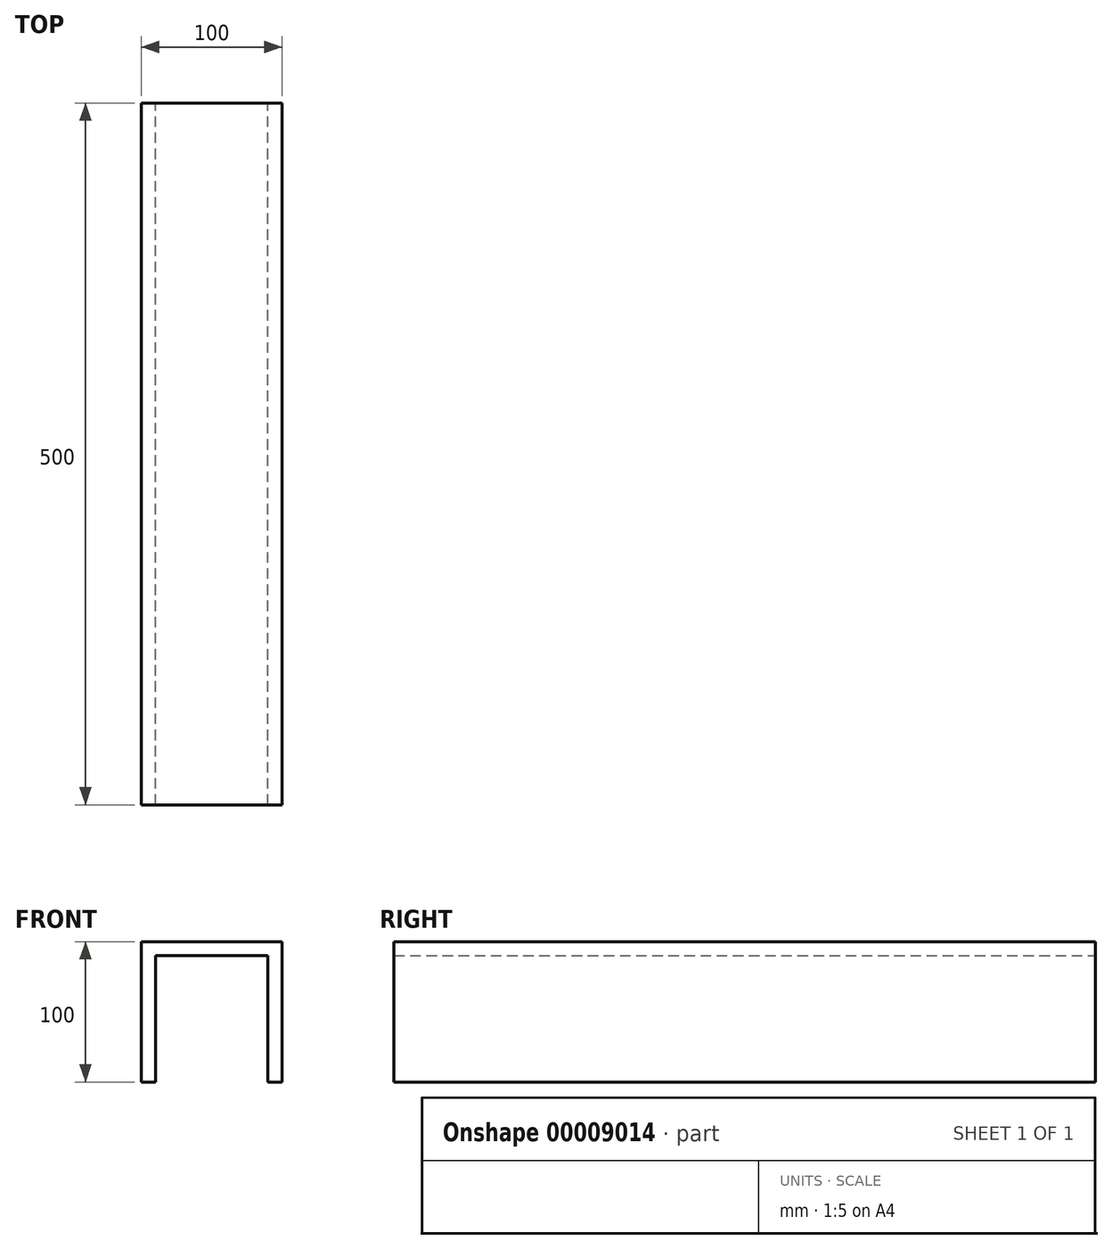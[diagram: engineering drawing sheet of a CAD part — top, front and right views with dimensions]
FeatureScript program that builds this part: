
annotation { "Feature Type Name" : "Feature", "Feature Type Description" : "" }
export const myFeature = defineFeature(function(context is Context, id is Id, definition is map)
    precondition{}
    {
        {
            var Q0;
            Q0=qCreatedBy(makeId("Front.planeOp"),FACE);
            var sketch = newSketch(context, id + "F0", { "sketchPlane" : qUnion([Q0])});
            skLineSegment(sketch, "E0.rect.bottom", {"start": v(50, 100) * mm, "end": v(-50, 100) * mm});
            skLineSegment(sketch, "E0.rect.left", {"start": v(50, 100) * mm, "end": v(50, 0) * mm});
            skLineSegment(sketch, "E0.rect.right", {"start": v(-50, 100) * mm, "end": v(-50, 0) * mm});
            skPoint(sketch, "E0.rect.middle", {"position": v(0, 0) * mm});
            skLineSegment(sketch, "E1.rect.bottom", {"start": v(40, 90) * mm, "end": v(-40, 90) * mm});
            skLineSegment(sketch, "E1.rect.left", {"start": v(40, 90) * mm, "end": v(40, 0) * mm});
            skLineSegment(sketch, "E1.rect.right", {"start": v(-40, 90) * mm, "end": v(-40, 0) * mm});
            skLineSegment(sketch, "E2", {"start": v(-50, 0) * mm, "end": v(-40, 0) * mm});
            skLineSegment(sketch, "E3", {"start": v(40, 0) * mm, "end": v(50, 0) * mm});
            skPoint(sketch, "E1.rect.top.end.orphan", {"position": v(-40, -90) * mm});
            skPoint(sketch, "E1.rect.top.start.orphan", {"position": v(40, -90) * mm});
            skPoint(sketch, "E0.rect.top.end.orphan", {"position": v(-50, -100) * mm});
            skPoint(sketch, "E0.rect.top.start.orphan", {"position": v(50, -100) * mm});
            skSolve(sketch);
        }
        {
            var Q0;
            Q0 = qSketchRegion(id + "F0", true);
            extrude(context, id + "F1", {"entities" : qUnion([Q0]), "endBound" : BoundingType.SYMMETRIC, "depth" : 500 * mm});
        }
    });
